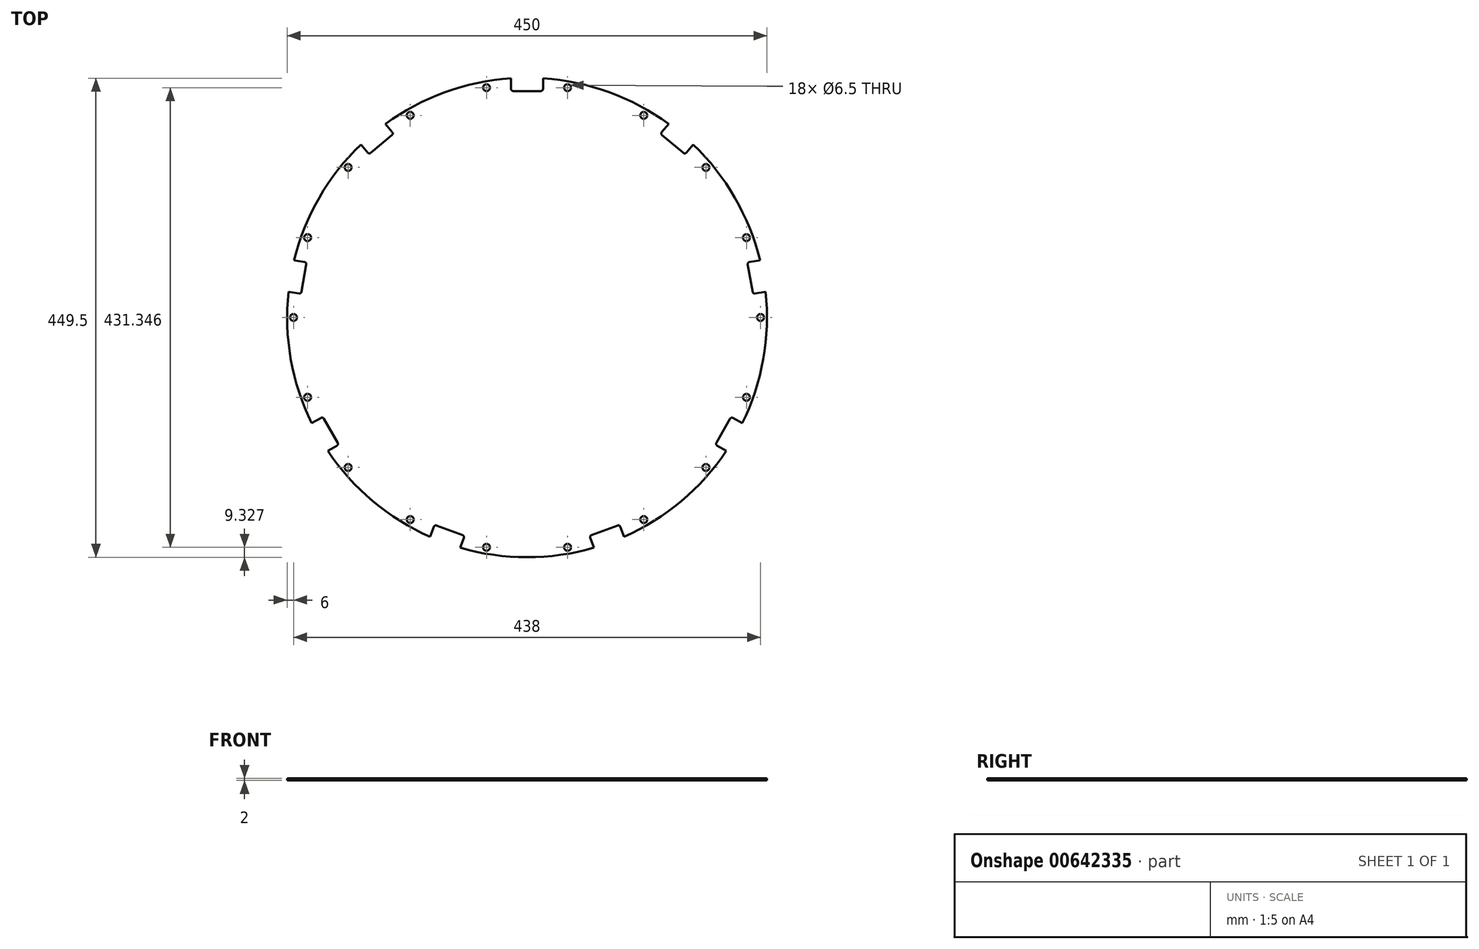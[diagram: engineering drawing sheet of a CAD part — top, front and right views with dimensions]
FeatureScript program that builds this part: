
annotation { "Feature Type Name" : "Feature", "Feature Type Description" : "" }
export const myFeature = defineFeature(function(context is Context, id is Id, definition is map)
    precondition{}
    {
        {
            var Q0;
            Q0=qCreatedBy(makeId("Top.planeOp"),FACE);
            var sketch = newSketch(context, id + "F0", { "sketchPlane" : qUnion([Q0])});
            skCircle(sketch, "E0", {"center": v(0, 0) * mm, "radius": 225 * mm});
            skSolve(sketch);
        }
        {
            var Q0;
            Q0=makeQuery(id+"F0.imprint","IMPRINT",FACE,{"disambiguationData":[TD([[makeQuery(id+"F0.imprint","IMPRINT",EDGE,{"derivedFrom":sQuery(id+"F0.wireOp",EDGE,"E0")}),1.0]])]});
            extrude(context, id + "F1", {"entities" : qUnion([Q0]), "depth" : 2 * mm, "offsetDistance" : 25 * mm});
        }
        {
            var Q0;
            Q0=makeQuery(id+"F1.opExtrude","CAP_FACE",FACE,{"disambiguationData":[OSD([sQuery(id+"F0.wireOp",EDGE,"E0")])],"isStart":false});
            var sketch = newSketch(context, id + "F2", { "sketchPlane" : qUnion([Q0])});
            skPoint(sketch, "E1", {"position": v(219, 0) * mm});
            skPoint(sketch, "E2.1.0", {"position": v(205.8, 74.9) * mm});
            skPoint(sketch, "E2.2.0", {"position": v(167.76, 140.77) * mm});
            skPoint(sketch, "E2.3.0", {"position": v(109.5, 189.66) * mm});
            skPoint(sketch, "E2.4.0", {"position": v(38.03, 215.67) * mm});
            skPoint(sketch, "E2.5.0", {"position": v(-38.03, 215.67) * mm});
            skPoint(sketch, "E2.6.0", {"position": v(-109.5, 189.66) * mm});
            skPoint(sketch, "E2.7.0", {"position": v(-167.76, 140.77) * mm});
            skPoint(sketch, "E2.8.0", {"position": v(-205.8, 74.9) * mm});
            skPoint(sketch, "E2.9.0", {"position": v(-219, 0) * mm});
            skPoint(sketch, "E2.10.0", {"position": v(-205.8, -74.9) * mm});
            skPoint(sketch, "E2.11.0", {"position": v(-167.76, -140.77) * mm});
            skPoint(sketch, "E2.12.0", {"position": v(-109.5, -189.66) * mm});
            skPoint(sketch, "E2.13.0", {"position": v(-38.03, -215.67) * mm});
            skPoint(sketch, "E2.14.0", {"position": v(38.03, -215.67) * mm});
            skPoint(sketch, "E2.15.0", {"position": v(109.5, -189.66) * mm});
            skPoint(sketch, "E2.16.0", {"position": v(167.76, -140.77) * mm});
            skPoint(sketch, "E2.17.0", {"position": v(205.8, -74.9) * mm});
            skPoint(sketch, "E2.center", {"position": v(0, 0) * mm});
            skSolve(sketch);
        }
        {
            var Q0;
            Q0=sQuery(id+"F2.wireOp",VERTEX,"E1");
            var Q1;
            Q1=sQuery(id+"F2.wireOp",VERTEX,"E2.1.0");
            var Q2;
            Q2=sQuery(id+"F2.wireOp",VERTEX,"E2.2.0");
            var Q3;
            Q3=sQuery(id+"F2.wireOp",VERTEX,"E2.3.0");
            var Q4;
            Q4=sQuery(id+"F2.wireOp",VERTEX,"E2.4.0");
            var Q5;
            Q5=sQuery(id+"F2.wireOp",VERTEX,"E2.5.0");
            var Q6;
            Q6=sQuery(id+"F2.wireOp",VERTEX,"E2.6.0");
            var Q7;
            Q7=sQuery(id+"F2.wireOp",VERTEX,"E2.7.0");
            var Q8;
            Q8=sQuery(id+"F2.wireOp",VERTEX,"E2.8.0");
            var Q9;
            Q9=sQuery(id+"F2.wireOp",VERTEX,"E2.9.0");
            var Q10;
            Q10=sQuery(id+"F2.wireOp",VERTEX,"E2.10.0");
            var Q11;
            Q11=sQuery(id+"F2.wireOp",VERTEX,"E2.11.0");
            var Q12;
            Q12=sQuery(id+"F2.wireOp",VERTEX,"E2.12.0");
            var Q13;
            Q13=sQuery(id+"F2.wireOp",VERTEX,"E2.13.0");
            var Q14;
            Q14=sQuery(id+"F2.wireOp",VERTEX,"E2.14.0");
            var Q15;
            Q15=sQuery(id+"F2.wireOp",VERTEX,"E2.15.0");
            var Q16;
            Q16=sQuery(id+"F2.wireOp",VERTEX,"E2.16.0");
            var Q17;
            Q17=sQuery(id+"F2.wireOp",VERTEX,"E2.17.0");
            var Q18;
            Q18=sQuery(id+"F2.wireOp",VERTEX,"E2.18.0");
            var Q19;
            Q19=sQuery(id+"F2.wireOp",VERTEX,"E2.19.0");
            var Q20;
            Q20=sQuery(id+"F2.wireOp",VERTEX,"E2.20.0");
            var Q21;
            Q21=sQuery(id+"F2.wireOp",VERTEX,"E2.21.0");
            var Q22;
            Q22=sQuery(id+"F2.wireOp",VERTEX,"E2.22.0");
            var Q23;
            Q23=sQuery(id+"F2.wireOp",VERTEX,"E2.23.0");
            var Q24;
            Q24=sQuery(id+"F2.wireOp",VERTEX,"E2.24.0");
            var Q25;
            Q25=sQuery(id+"F2.wireOp",VERTEX,"E2.25.0");
            var Q26;
            Q26=sQuery(id+"F2.wireOp",VERTEX,"E2.26.0");
            var Q27;
            Q27=sQuery(id+"F2.wireOp",VERTEX,"E2.27.0");
            var Q28;
            Q28=sQuery(id+"F2.wireOp",VERTEX,"E2.28.0");
            var Q29;
            Q29=sQuery(id+"F2.wireOp",VERTEX,"E2.29.0");
            var Q30;
            Q30=sQuery(id+"F2.wireOp",VERTEX,"E2.30.0");
            var Q31;
            Q31=sQuery(id+"F2.wireOp",VERTEX,"E2.31.0");
            var Q32;
            Q32=sQuery(id+"F2.wireOp",VERTEX,"E2.32.0");
            var Q33;
            Q33=sQuery(id+"F2.wireOp",VERTEX,"E2.33.0");
            var Q34;
            Q34=sQuery(id+"F2.wireOp",VERTEX,"E2.34.0");
            var Q35;
            Q35=sQuery(id+"F2.wireOp",VERTEX,"E2.35.0");
            var Q36;
            Q36=makeQuery(id+"F1.opExtrude","SWEPT_BODY",BODY,{"disambiguationData":[OSD([sQuery(id+"F0.wireOp",EDGE,"E0")])]});
            hole(context, id + "F3", {"style" : HoleStyle.SIMPLE, "endStyle" : HoleEndStyle.THROUGH, "holeDiameter" : 6.5 * mm, "majorDiameter" : 5 * mm, "isTappedThrough" : true, "tappedDepth" : 12 * mm, "tapClearance" : 3, "locations" : qUnion([Q0, Q1, Q2, Q3, Q4, Q5, Q6, Q7, Q8, Q9, Q10, Q11, Q12, Q13, Q14, Q15, Q16, Q17, Q18, Q19, Q20, Q21, Q22, Q23, Q24, Q25, Q26, Q27, Q28, Q29, Q30, Q31, Q32, Q33, Q34, Q35]), "scope" : qUnion([Q36])});
        }
        {
            var Q0;
            Q0=makeQuery(id+"F1.opExtrude","CAP_FACE",FACE,{"disambiguationData":[OSD([sQuery(id+"F0.wireOp",EDGE,"E0")])],"isStart":false});
            var sketch = newSketch(context, id + "F4", { "sketchPlane" : qUnion([Q0])});
            skLineSegment(sketch, "E3", {"start": v(0, 0) * mm, "end": v(221.58, 39.07) * mm, "construction": true});
            skLineSegment(sketch, "E4", {"start": v(218.48, 53.76) * mm, "end": v(208.64, 52.02) * mm});
            skLineSegment(sketch, "E5", {"start": v(207.01, 49.7) * mm, "end": v(209.27, 36.9) * mm});
            skLineSegment(sketch, "E6", {"start": v(209.27, 36.9) * mm, "end": v(211.53, 24.1) * mm});
            skLineSegment(sketch, "E7", {"start": v(213.85, 22.48) * mm, "end": v(223.7, 24.21) * mm});
            skPoint(sketch, "E8.center", {"position": v(0, 0) * mm});
            skPoint(sketch, "E9.visualSharp", {"position": v(206.67, 51.67) * mm});
            skArc(sketch, "E9.filletArc", {"start": v(208.64, 52.02) * mm, "mid": v(207.34, 51.2) * mm, "end": v(207.01, 49.7) * mm});
            skPoint(sketch, "E10.visualSharp", {"position": v(211.88, 22.13) * mm});
            skArc(sketch, "E10.filletArc", {"start": v(211.53, 24.1) * mm, "mid": v(212.35, 22.8) * mm, "end": v(213.85, 22.48) * mm});
            skLineSegment(sketch, "E11.1.0", {"start": v(132.81, 181.62) * mm, "end": v(126.39, 173.96) * mm});
            skPoint(sketch, "E11.1.1", {"position": v(148.08, 153.14) * mm});
            skLineSegment(sketch, "E11.1.2", {"start": v(136.6, 162.78) * mm, "end": v(146.55, 154.43) * mm});
            skLineSegment(sketch, "E11.1.3", {"start": v(149.37, 154.67) * mm, "end": v(155.8, 162.33) * mm});
            skLineSegment(sketch, "E11.1.4", {"start": v(0, 0) * mm, "end": v(144.63, 172.36) * mm, "construction": true});
            skLineSegment(sketch, "E11.1.5", {"start": v(126.63, 171.14) * mm, "end": v(136.6, 162.78) * mm});
            skPoint(sketch, "E11.1.6", {"position": v(125.1, 172.43) * mm});
            skArc(sketch, "E11.1.7", {"start": v(126.39, 173.96) * mm, "mid": v(125.93, 172.5) * mm, "end": v(126.63, 171.14) * mm});
            skArc(sketch, "E11.1.8", {"start": v(146.55, 154.43) * mm, "mid": v(148.01, 153.97) * mm, "end": v(149.37, 154.67) * mm});
            skLineSegment(sketch, "E11.2.0", {"start": v(-15, 224.5) * mm, "end": v(-15, 214.5) * mm});
            skPoint(sketch, "E11.2.1", {"position": v(15, 212.5) * mm});
            skLineSegment(sketch, "E11.2.2", {"start": v(0, 212.5) * mm, "end": v(13, 212.5) * mm});
            skLineSegment(sketch, "E11.2.3", {"start": v(15, 214.5) * mm, "end": v(15, 224.5) * mm});
            skLineSegment(sketch, "E11.2.4", {"start": v(0, 0) * mm, "end": v(0, 225) * mm, "construction": true});
            skLineSegment(sketch, "E11.2.5", {"start": v(-13, 212.5) * mm, "end": v(0, 212.5) * mm});
            skPoint(sketch, "E11.2.6", {"position": v(-15, 212.5) * mm});
            skArc(sketch, "E11.2.7", {"start": v(-15, 214.5) * mm, "mid": v(-14.41, 213.09) * mm, "end": v(-13, 212.5) * mm});
            skArc(sketch, "E11.2.8", {"start": v(13, 212.5) * mm, "mid": v(14.41, 213.09) * mm, "end": v(15, 214.5) * mm});
            skLineSegment(sketch, "E11.3.0", {"start": v(-155.8, 162.33) * mm, "end": v(-149.37, 154.67) * mm});
            skPoint(sketch, "E11.3.1", {"position": v(-125.1, 172.43) * mm});
            skLineSegment(sketch, "E11.3.2", {"start": v(-136.6, 162.78) * mm, "end": v(-126.63, 171.14) * mm});
            skLineSegment(sketch, "E11.3.3", {"start": v(-126.39, 173.96) * mm, "end": v(-132.81, 181.62) * mm});
            skLineSegment(sketch, "E11.3.4", {"start": v(0, 0) * mm, "end": v(-144.63, 172.36) * mm, "construction": true});
            skLineSegment(sketch, "E11.3.5", {"start": v(-146.55, 154.43) * mm, "end": v(-136.6, 162.78) * mm});
            skPoint(sketch, "E11.3.6", {"position": v(-148.08, 153.14) * mm});
            skArc(sketch, "E11.3.7", {"start": v(-149.37, 154.67) * mm, "mid": v(-148.01, 153.97) * mm, "end": v(-146.55, 154.43) * mm});
            skArc(sketch, "E11.3.8", {"start": v(-126.63, 171.14) * mm, "mid": v(-125.93, 172.5) * mm, "end": v(-126.39, 173.96) * mm});
            skLineSegment(sketch, "E11.4.0", {"start": v(-223.7, 24.21) * mm, "end": v(-213.85, 22.48) * mm});
            skPoint(sketch, "E11.4.1", {"position": v(-206.67, 51.67) * mm});
            skLineSegment(sketch, "E11.4.2", {"start": v(-209.27, 36.9) * mm, "end": v(-207.01, 49.7) * mm});
            skLineSegment(sketch, "E11.4.3", {"start": v(-208.64, 52.02) * mm, "end": v(-218.48, 53.76) * mm});
            skLineSegment(sketch, "E11.4.4", {"start": v(0, 0) * mm, "end": v(-221.58, 39.07) * mm, "construction": true});
            skLineSegment(sketch, "E11.4.5", {"start": v(-211.53, 24.1) * mm, "end": v(-209.27, 36.9) * mm});
            skPoint(sketch, "E11.4.6", {"position": v(-211.88, 22.13) * mm});
            skArc(sketch, "E11.4.7", {"start": v(-213.85, 22.48) * mm, "mid": v(-212.35, 22.8) * mm, "end": v(-211.53, 24.1) * mm});
            skArc(sketch, "E11.4.8", {"start": v(-207.01, 49.7) * mm, "mid": v(-207.34, 51.2) * mm, "end": v(-208.64, 52.02) * mm});
            skLineSegment(sketch, "E11.5.0", {"start": v(-186.92, -125.24) * mm, "end": v(-178.26, -120.24) * mm});
            skPoint(sketch, "E11.5.1", {"position": v(-191.53, -93.26) * mm});
            skLineSegment(sketch, "E11.5.2", {"start": v(-184.03, -106.25) * mm, "end": v(-190.53, -95) * mm});
            skLineSegment(sketch, "E11.5.3", {"start": v(-193.26, -94.26) * mm, "end": v(-201.92, -99.26) * mm});
            skLineSegment(sketch, "E11.5.4", {"start": v(0, 0) * mm, "end": v(-194.86, -112.5) * mm, "construction": true});
            skLineSegment(sketch, "E11.5.5", {"start": v(-177.53, -117.5) * mm, "end": v(-184.03, -106.25) * mm});
            skPoint(sketch, "E11.5.6", {"position": v(-176.53, -119.24) * mm});
            skArc(sketch, "E11.5.7", {"start": v(-178.26, -120.24) * mm, "mid": v(-177.33, -119.03) * mm, "end": v(-177.53, -117.5) * mm});
            skArc(sketch, "E11.5.8", {"start": v(-190.53, -95) * mm, "mid": v(-191.74, -94.06) * mm, "end": v(-193.26, -94.26) * mm});
            skLineSegment(sketch, "E11.6.0", {"start": v(-62.69, -216.1) * mm, "end": v(-59.27, -206.7) * mm});
            skPoint(sketch, "E11.6.1", {"position": v(-86.77, -194.55) * mm});
            skLineSegment(sketch, "E11.6.2", {"start": v(-72.68, -199.68) * mm, "end": v(-84.9, -195.24) * mm});
            skLineSegment(sketch, "E11.6.3", {"start": v(-87.46, -196.43) * mm, "end": v(-90.88, -205.83) * mm});
            skLineSegment(sketch, "E11.6.4", {"start": v(0, 0) * mm, "end": v(-76.95, -211.43) * mm, "construction": true});
            skLineSegment(sketch, "E11.6.5", {"start": v(-60.46, -204.13) * mm, "end": v(-72.68, -199.68) * mm});
            skPoint(sketch, "E11.6.6", {"position": v(-58.58, -204.81) * mm});
            skArc(sketch, "E11.6.7", {"start": v(-59.27, -206.7) * mm, "mid": v(-59.33, -205.16) * mm, "end": v(-60.46, -204.13) * mm});
            skArc(sketch, "E11.6.8", {"start": v(-84.9, -195.24) * mm, "mid": v(-86.42, -195.3) * mm, "end": v(-87.46, -196.43) * mm});
            skLineSegment(sketch, "E11.7.0", {"start": v(90.88, -205.83) * mm, "end": v(87.46, -196.43) * mm});
            skPoint(sketch, "E11.7.1", {"position": v(58.58, -204.81) * mm});
            skLineSegment(sketch, "E11.7.2", {"start": v(72.68, -199.68) * mm, "end": v(60.46, -204.13) * mm});
            skLineSegment(sketch, "E11.7.3", {"start": v(59.27, -206.7) * mm, "end": v(62.69, -216.1) * mm});
            skLineSegment(sketch, "E11.7.4", {"start": v(0, 0) * mm, "end": v(76.95, -211.43) * mm, "construction": true});
            skLineSegment(sketch, "E11.7.5", {"start": v(84.9, -195.24) * mm, "end": v(72.68, -199.68) * mm});
            skPoint(sketch, "E11.7.6", {"position": v(86.77, -194.55) * mm});
            skArc(sketch, "E11.7.7", {"start": v(87.46, -196.43) * mm, "mid": v(86.42, -195.3) * mm, "end": v(84.9, -195.24) * mm});
            skArc(sketch, "E11.7.8", {"start": v(60.46, -204.13) * mm, "mid": v(59.33, -205.16) * mm, "end": v(59.27, -206.7) * mm});
            skLineSegment(sketch, "E11.8.0", {"start": v(201.92, -99.26) * mm, "end": v(193.26, -94.26) * mm});
            skPoint(sketch, "E11.8.1", {"position": v(176.53, -119.24) * mm});
            skLineSegment(sketch, "E11.8.2", {"start": v(184.03, -106.25) * mm, "end": v(177.53, -117.5) * mm});
            skLineSegment(sketch, "E11.8.3", {"start": v(178.26, -120.24) * mm, "end": v(186.92, -125.24) * mm});
            skLineSegment(sketch, "E11.8.4", {"start": v(0, 0) * mm, "end": v(194.86, -112.5) * mm, "construction": true});
            skLineSegment(sketch, "E11.8.5", {"start": v(190.53, -95) * mm, "end": v(184.03, -106.25) * mm});
            skPoint(sketch, "E11.8.6", {"position": v(191.53, -93.26) * mm});
            skArc(sketch, "E11.8.7", {"start": v(193.26, -94.26) * mm, "mid": v(191.74, -94.06) * mm, "end": v(190.53, -95) * mm});
            skArc(sketch, "E11.8.8", {"start": v(177.53, -117.5) * mm, "mid": v(177.33, -119.03) * mm, "end": v(178.26, -120.24) * mm});
            skSolve(sketch);
        }
        {
            var Q0;
            {var subQ1=sQuery(id+"F4.wireOp",EDGE,"E4");Q0=makeQuery(id+"F4.imprint","IMPRINT",FACE,{"disambiguationData":[TD([[makeQuery(id+"F4.imprint","IMPRINT",EDGE,{"derivedFrom":subQ1}),1.0]])]});}
            var Q1;
            {var subQ0=sQuery(id+"F4.wireOp",EDGE,"E11.1.0");Q1=makeQuery(id+"F4.imprint","IMPRINT",FACE,{"disambiguationData":[TD([[makeQuery(id+"F4.imprint","IMPRINT",EDGE,{"derivedFrom":subQ0}),1.0]])]});}
            var Q2;
            {var subQ1=sQuery(id+"F4.wireOp",EDGE,"E11.2.0");Q2=makeQuery(id+"F4.imprint","IMPRINT",FACE,{"disambiguationData":[TD([[makeQuery(id+"F4.imprint","IMPRINT",EDGE,{"derivedFrom":subQ1}),1.0]])]});}
            var Q3;
            {var subQ1=sQuery(id+"F4.wireOp",EDGE,"E11.3.0");Q3=makeQuery(id+"F4.imprint","IMPRINT",FACE,{"disambiguationData":[TD([[makeQuery(id+"F4.imprint","IMPRINT",EDGE,{"derivedFrom":subQ1}),1.0]])]});}
            var Q4;
            {var subQ1=sQuery(id+"F4.wireOp",EDGE,"E11.4.0");Q4=makeQuery(id+"F4.imprint","IMPRINT",FACE,{"disambiguationData":[TD([[makeQuery(id+"F4.imprint","IMPRINT",EDGE,{"derivedFrom":subQ1}),1.0]])]});}
            var Q5;
            {var subQ1=sQuery(id+"F4.wireOp",EDGE,"E11.5.0");Q5=makeQuery(id+"F4.imprint","IMPRINT",FACE,{"disambiguationData":[TD([[makeQuery(id+"F4.imprint","IMPRINT",EDGE,{"derivedFrom":subQ1}),1.0]])]});}
            var Q6;
            {var subQ1=sQuery(id+"F4.wireOp",EDGE,"E11.6.0");Q6=makeQuery(id+"F4.imprint","IMPRINT",FACE,{"disambiguationData":[TD([[makeQuery(id+"F4.imprint","IMPRINT",EDGE,{"derivedFrom":subQ1}),1.0]])]});}
            var Q7;
            {var subQ1=sQuery(id+"F4.wireOp",EDGE,"E11.7.0");Q7=makeQuery(id+"F4.imprint","IMPRINT",FACE,{"disambiguationData":[TD([[makeQuery(id+"F4.imprint","IMPRINT",EDGE,{"derivedFrom":subQ1}),1.0]])]});}
            var Q8;
            {var subQ1=sQuery(id+"F4.wireOp",EDGE,"E11.8.0");Q8=makeQuery(id+"F4.imprint","IMPRINT",FACE,{"disambiguationData":[TD([[makeQuery(id+"F4.imprint","IMPRINT",EDGE,{"derivedFrom":subQ1}),1.0]])]});}
            extrude(context, id + "F5", {"entities" : qUnion([Q0, Q1, Q2, Q3, Q4, Q5, Q6, Q7, Q8]), "operationType" : NewBodyOperationType.REMOVE, "endBound" : BoundingType.THROUGH_ALL, "oppositeDirection" : true, "depth" : 25 * mm, "offsetDistance" : 25 * mm});
        }
    });
